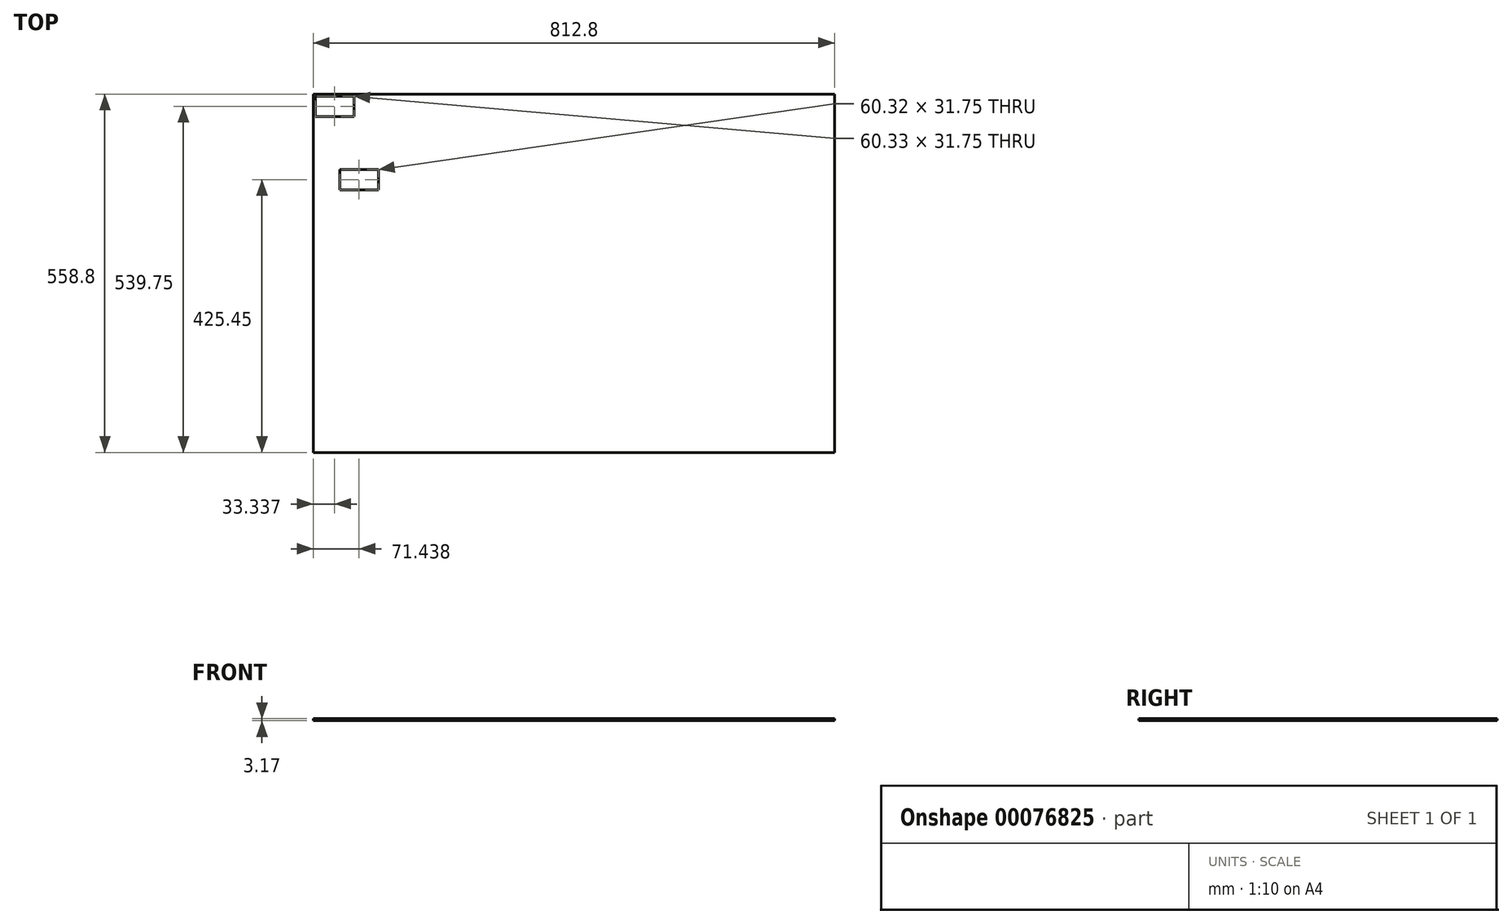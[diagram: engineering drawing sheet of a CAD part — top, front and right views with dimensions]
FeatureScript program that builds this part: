
annotation { "Feature Type Name" : "Feature", "Feature Type Description" : "" }
export const myFeature = defineFeature(function(context is Context, id is Id, definition is map)
    precondition{}
    {
        {
            var Q0;
            Q0=qCreatedBy(makeId("Top.planeOp"),FACE);
            var sketch = newSketch(context, id + "F0", { "sketchPlane" : qUnion([Q0])});
            skLineSegment(sketch, "E0.bottom", {"start": v(406.4, -279.4) * mm, "end": v(-406.4, -279.4) * mm});
            skLineSegment(sketch, "E0.top", {"start": v(406.4, 279.4) * mm, "end": v(-406.4, 279.4) * mm});
            skLineSegment(sketch, "E0.left", {"start": v(406.4, -279.4) * mm, "end": v(406.4, 279.4) * mm});
            skLineSegment(sketch, "E0.right", {"start": v(-406.4, -279.4) * mm, "end": v(-406.4, 279.4) * mm});
            skPoint(sketch, "E0.middle", {"position": v(0, 0) * mm});
            skSolve(sketch);
        }
        {
            var Q0;
            Q0 = qSketchRegion(id + "F0", true);
            extrude(context, id + "F1", {"entities" : qUnion([Q0]), "depth" : 3.17 * mm});
        }
        {
            var Q0;
            Q0=makeQuery(id+"F1.opExtrude","CAP_FACE",FACE,{"disambiguationData":[OSD([sQuery(id+"F0.wireOp",EDGE,"E0.bottom"),sQuery(id+"F0.wireOp",EDGE,"E0.top"),sQuery(id+"F0.wireOp",EDGE,"E0.left"),sQuery(id+"F0.wireOp",EDGE,"E0.right")])],"isStart":false});
            var sketch = newSketch(context, id + "F2", { "sketchPlane" : qUnion([Q0])});
            skLineSegment(sketch, "E1.bottom", {"start": v(-365.12, 161.92) * mm, "end": v(-304.8, 161.92) * mm});
            skLineSegment(sketch, "E1.top", {"start": v(-365.12, 130.17) * mm, "end": v(-304.8, 130.17) * mm});
            skLineSegment(sketch, "E1.left", {"start": v(-365.12, 161.92) * mm, "end": v(-365.12, 130.17) * mm});
            skLineSegment(sketch, "E1.right", {"start": v(-304.8, 161.92) * mm, "end": v(-304.8, 130.17) * mm});
            skLineSegment(sketch, "E2.bottom", {"start": v(-403.23, 276.23) * mm, "end": v(-342.9, 276.23) * mm});
            skLineSegment(sketch, "E2.top", {"start": v(-403.23, 244.47) * mm, "end": v(-342.9, 244.47) * mm});
            skLineSegment(sketch, "E2.left", {"start": v(-403.23, 276.23) * mm, "end": v(-403.23, 244.47) * mm});
            skLineSegment(sketch, "E2.right", {"start": v(-342.9, 276.23) * mm, "end": v(-342.9, 244.47) * mm});
            skSolve(sketch);
        }
        {
            var Q0;
            Q0=makeQuery(id+"F2.imprint","IMPRINT",FACE,{"disambiguationData":[TD([[makeQuery(id+"F2.imprint","IMPRINT",EDGE,{"derivedFrom":sQuery(id+"F2.wireOp",EDGE,"E2.bottom")}),-1.0]])]});
            var Q1;
            Q1=makeQuery(id+"F2.imprint","IMPRINT",FACE,{"disambiguationData":[TD([[makeQuery(id+"F2.imprint","IMPRINT",EDGE,{"derivedFrom":sQuery(id+"F2.wireOp",EDGE,"E1.bottom")}),-1.0]])]});
            extrude(context, id + "F3", {"entities" : qUnion([Q0, Q1]), "operationType" : NewBodyOperationType.REMOVE, "endBound" : BoundingType.THROUGH_ALL, "oppositeDirection" : true, "depth" : 25.4 * mm});
        }
    });
